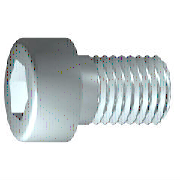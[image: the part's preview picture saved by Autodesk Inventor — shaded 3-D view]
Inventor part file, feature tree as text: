
AUTODESK INVENTOR PART (.ipt)
format: ipt  version: 2022 (Build 260153000, 153)  size: 182,272 bytes
history: native  units: mm (DEFAULTED — no unit token found)
features: sketch x2, extrude x1, plane x1
ambient origin geometry x7: Origin, YZ Plane, XY Plane, X Axis, Y Axis, Z Axis, Center Point
bodies: Solid1 (feature_tree), Body (feature_tree)
feature tree (4):
  extrude  "Slot"  Depth=0.429415mm
  plane  "Work Plane1"
  sketch  "Sketch1"  dims[d0=20.0mm d1=0.429415mm]
  sketch  "Sketch2"  dims[d2=4.0mm d3=2.0mm d4=60.0deg d5=4.0mm d6=4.0mm d7=3.464102mm d8=7.0mm d10=90.0deg d11=10.0mm d9=0.0mm d12=20.0mm d13=0.0mm d14=0.429415mm d15=0.429415mm d16=0.4mm d17=0.0mm d18=0.0mm d19=50.0mm d27=45.0deg d28=0.2mm d29=0.2mm]
